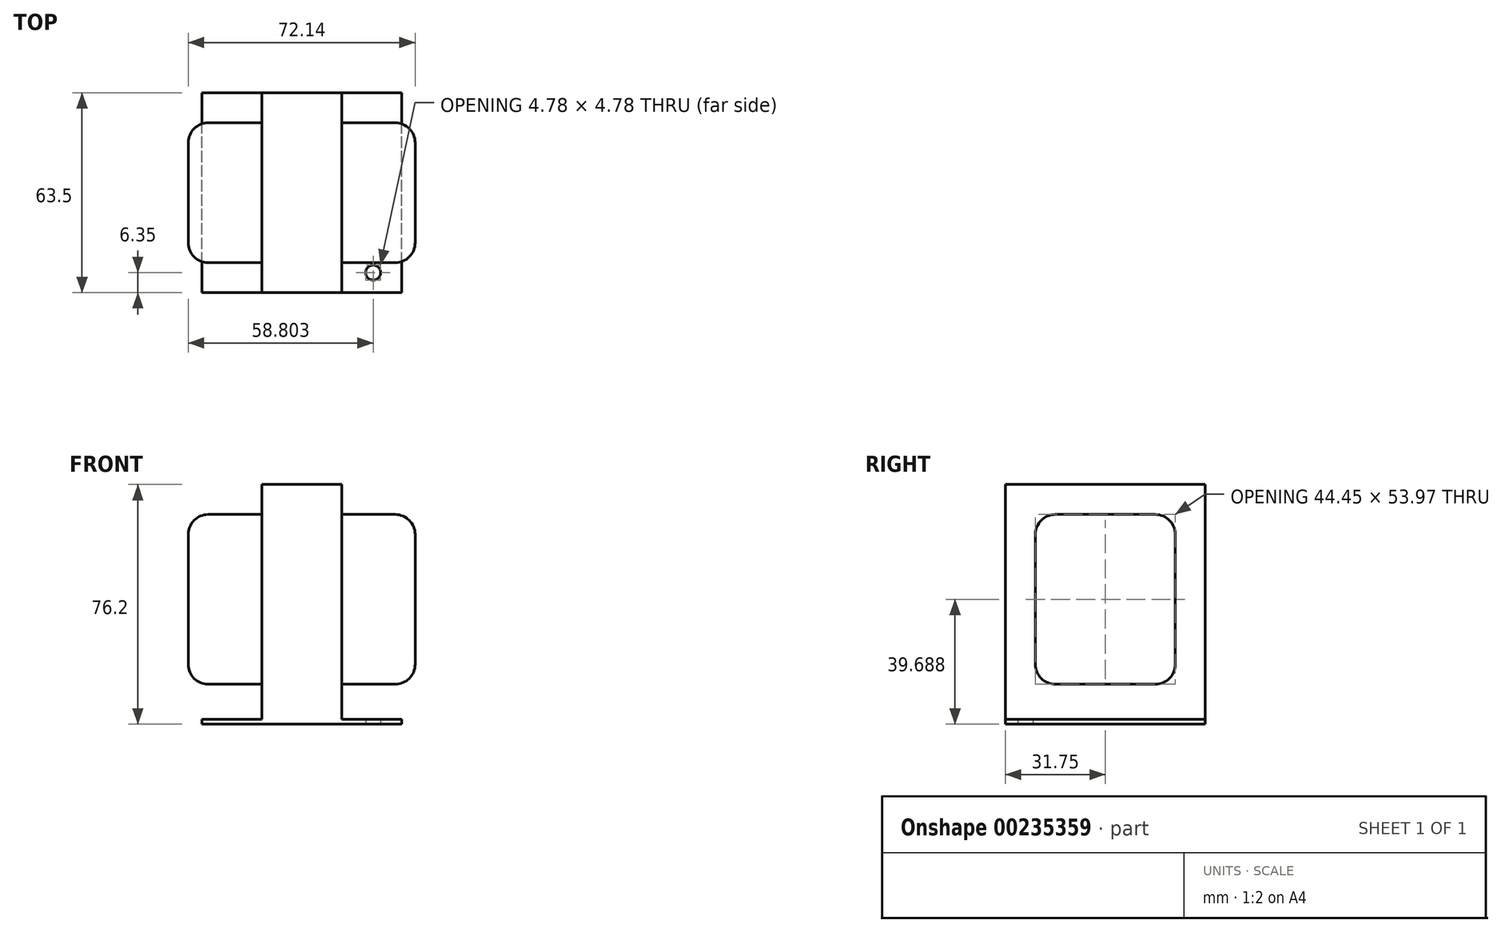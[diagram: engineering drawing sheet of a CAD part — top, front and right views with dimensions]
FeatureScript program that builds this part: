
annotation { "Feature Type Name" : "Feature", "Feature Type Description" : "" }
export const myFeature = defineFeature(function(context is Context, id is Id, definition is map)
    precondition{}
    {
        {
            var Q0;
            Q0=qCreatedBy(makeId("Front.planeOp"),FACE);
            var sketch = newSketch(context, id + "F0", { "sketchPlane" : qUnion([Q0])});
            skPoint(sketch, "E0.0", {"position": v(0, 0) * mm});
            skLineSegment(sketch, "E1.bottom", {"start": v(0, 0) * mm, "end": v(-31.75, 0) * mm});
            skLineSegment(sketch, "E1.top", {"start": v(0, 1.52) * mm, "end": v(-31.75, 1.52) * mm});
            skLineSegment(sketch, "E1.left", {"start": v(0, 0) * mm, "end": v(0, 1.52) * mm});
            skLineSegment(sketch, "E1.right", {"start": v(-31.75, 0) * mm, "end": v(-31.75, 1.52) * mm});
            skLineSegment(sketch, "E2.bottom", {"start": v(0, 0) * mm, "end": v(-12.7, 0) * mm});
            skLineSegment(sketch, "E2.top", {"start": v(0, 76.2) * mm, "end": v(-12.7, 76.2) * mm});
            skLineSegment(sketch, "E2.left", {"start": v(0, 0) * mm, "end": v(0, 76.2) * mm});
            skLineSegment(sketch, "E2.right", {"start": v(-12.7, 0) * mm, "end": v(-12.7, 76.2) * mm});
            skSolve(sketch);
        }
        {
            var Q0;
            {var subQ5=sQuery(id+"F0.wireOp",EDGE,"E2.top");Q0=makeQuery(id+"F0.imprint","IMPRINT",FACE,{"disambiguationData":[TD([[makeQuery(id+"F0.imprint","IMPRINT",EDGE,{"derivedFrom":subQ5}),1.0]])]});}
            var Q1;
            {var subQ0=sQuery(id+"F0.wireOp",EDGE,"E1.bottom");Q1=makeQuery(id+"F0.imprint","IMPRINT",FACE,{"disambiguationData":[TD([[makeQuery(id+"F0.imprint","IMPRINT",EDGE,{"derivedFrom":subQ0}),-1.0]])]});}
            var Q2;
            {var subQ5=sQuery(id+"F0.wireOp",EDGE,"E2.bottom");Q2=makeQuery(id+"F0.imprint","IMPRINT",FACE,{"disambiguationData":[TD([[makeQuery(id+"F0.imprint","IMPRINT",EDGE,{"derivedFrom":subQ5}),-1.0]])]});}
            extrude(context, id + "F1", {"entities" : qUnion([Q0, Q1, Q2]), "endBound" : BoundingType.SYMMETRIC, "depth" : 63.5 * mm});
        }
        {
            var Q0;
            Q0=makeQuery(id+"F1.opExtrude","SWEPT_BODY",BODY,{"disambiguationData":[OSD([sQuery(id+"F0.wireOp",EDGE,"E1.bottom"),sQuery(id+"F0.wireOp",EDGE,"E1.top"),sQuery(id+"F0.wireOp",EDGE,"E1.right"),sQuery(id+"F0.wireOp",EDGE,"E2.bottom"),sQuery(id+"F0.wireOp",EDGE,"E2.top"),sQuery(id+"F0.wireOp",EDGE,"E2.left"),sQuery(id+"F0.wireOp",EDGE,"E2.right")])]});
            var Q1;
            Q1=qCreatedBy(makeId("Right.planeOp"),FACE);
            mirror(context, id + "F2", {"operationType" : NewBodyOperationType.ADD, "entities" : qUnion([Q0]), "mirrorPlane" : qUnion([Q1])});
        }
        {
            var Q0;
            Q0=qCreatedBy(makeId("Right.planeOp"),FACE);
            var sketch = newSketch(context, id + "F3", { "sketchPlane" : qUnion([Q0])});
            skLineSegment(sketch, "E3.bottom", {"start": v(-22.23, 66.67) * mm, "end": v(22.23, 66.67) * mm});
            skLineSegment(sketch, "E3.top", {"start": v(-22.22, 12.7) * mm, "end": v(22.23, 12.7) * mm});
            skLineSegment(sketch, "E3.left", {"start": v(-22.23, 66.67) * mm, "end": v(-22.22, 12.7) * mm});
            skLineSegment(sketch, "E3.right", {"start": v(22.23, 66.67) * mm, "end": v(22.23, 12.7) * mm});
            skSolve(sketch);
        }
        {
            var Q0;
            Q0 = qSketchRegion(id + "F3", true);
            extrude(context, id + "F4", {"entities" : qUnion([Q0]), "operationType" : NewBodyOperationType.ADD, "endBound" : BoundingType.SYMMETRIC, "depth" : 72.14 * mm});
        }
        {
            var Q0;
            {var subQ0=makeQuery(id+"F1.opExtrude","SWEPT_FACE",FACE,{"disambiguationData":[OSD([sQuery(id+"F0.wireOp",EDGE,"E1.bottom"),sQuery(id+"F0.wireOp",EDGE,"E2.bottom")])]});Q0=makeQuery(id+"F2.boolean.opBoolean","MERGE",FACE,{"derivedFrom":[subQ0,makeQuery(id+"F2.opPattern","COPY",FACE,{"derivedFrom":subQ0,"instanceName":"1"})]});}
            var sketch = newSketch(context, id + "F5", { "sketchPlane" : qUnion([Q0])});
            skLineSegment(sketch, "E4.0.1", {"start": v(31.75, -31.75) * mm, "end": v(31.75, 31.75) * mm});
            skLineSegment(sketch, "E4.0.2", {"start": v(31.75, 31.75) * mm, "end": v(-31.75, 31.75) * mm});
            skLineSegment(sketch, "E5", {"start": v(-31.75, 0) * mm, "end": v(31.75, 0) * mm, "construction": true});
            skLineSegment(sketch, "E6.bottom", {"start": v(22.74, 23.01) * mm, "end": v(22.73, 23.01) * mm});
            skLineSegment(sketch, "E6.top", {"start": v(22.74, 27.79) * mm, "end": v(22.73, 27.79) * mm});
            skLineSegment(sketch, "E6.left", {"start": v(25.12, 25.4) * mm, "end": v(25.12, 25.4) * mm});
            skLineSegment(sketch, "E6.right", {"start": v(20.35, 25.4) * mm, "end": v(20.35, 25.4) * mm});
            skPoint(sketch, "E6.middle", {"position": v(22.73, 25.4) * mm});
            skPoint(sketch, "E7.visualSharp", {"position": v(20.35, 23.01) * mm});
            skArc(sketch, "E7.filletArc", {"start": v(20.35, 25.4) * mm, "mid": v(21.04, 23.7) * mm, "end": v(22.73, 23.01) * mm});
            skPoint(sketch, "E8.visualSharp", {"position": v(20.35, 27.79) * mm});
            skArc(sketch, "E8.filletArc", {"start": v(22.73, 27.79) * mm, "mid": v(21.04, 27.1) * mm, "end": v(20.35, 25.4) * mm});
            skPoint(sketch, "E9.visualSharp", {"position": v(25.12, 27.79) * mm});
            skArc(sketch, "E9.filletArc", {"start": v(25.12, 25.4) * mm, "mid": v(24.42, 27.1) * mm, "end": v(22.74, 27.79) * mm});
            skPoint(sketch, "E10.visualSharp", {"position": v(25.12, 23.01) * mm});
            skArc(sketch, "E10.filletArc", {"start": v(22.74, 23.01) * mm, "mid": v(24.42, 23.7) * mm, "end": v(25.12, 25.4) * mm});
            skSolve(sketch);
        }
        {
            var Q0;
            Q0=makeQuery(id+"F5.imprint","IMPRINT",FACE,{"disambiguationData":[TD([[makeQuery(id+"F5.imprint","IMPRINT",EDGE,{"derivedFrom":sQuery(id+"F5.wireOp",EDGE,"E6.bottom")}),-1.0]])]});
            extrude(context, id + "F6", {"entities" : qUnion([Q0]), "operationType" : NewBodyOperationType.REMOVE, "endBound" : BoundingType.UP_TO_NEXT, "oppositeDirection" : true, "depth" : 25.4 * mm});
        }
        {
            var Q0;
            {var subQ0=sQuery(id+"F3.wireOp",EDGE,"E3.left");var subQ1=sQuery(id+"F3.wireOp",EDGE,"E3.bottom");Q0=makeQuery(id+"F4.boolean.opBoolean","SPLIT",EDGE,{"disambiguationData":[TD([makeQuery(id+"F2.opPattern","COPY",FACE,{"derivedFrom":makeQuery(id+"F1.opExtrude","SWEPT_FACE",FACE,{"disambiguationData":[OSD([sQuery(id+"F0.wireOp",EDGE,"E2.right")])]}),"instanceName":"1"})])],"derivedFrom":makeQuery(id+"F4.opExtrude","SWEPT_EDGE",EDGE,{"disambiguationData":[OSD([subQ1,subQ0])]})});}
            var Q1;
            {var subQ0=sQuery(id+"F3.wireOp",EDGE,"E3.right");var subQ1=sQuery(id+"F3.wireOp",EDGE,"E3.bottom");Q1=makeQuery(id+"F4.boolean.opBoolean","SPLIT",EDGE,{"disambiguationData":[TD([makeQuery(id+"F2.opPattern","COPY",FACE,{"derivedFrom":makeQuery(id+"F1.opExtrude","SWEPT_FACE",FACE,{"disambiguationData":[OSD([sQuery(id+"F0.wireOp",EDGE,"E2.right")])]}),"instanceName":"1"})])],"derivedFrom":makeQuery(id+"F4.opExtrude","SWEPT_EDGE",EDGE,{"disambiguationData":[OSD([subQ1,subQ0])]})});}
            var Q2;
            {var subQ0=sQuery(id+"F3.wireOp",EDGE,"E3.right");var subQ1=sQuery(id+"F3.wireOp",EDGE,"E3.top");Q2=makeQuery(id+"F4.boolean.opBoolean","SPLIT",EDGE,{"disambiguationData":[TD([makeQuery(id+"F2.opPattern","COPY",FACE,{"derivedFrom":makeQuery(id+"F1.opExtrude","SWEPT_FACE",FACE,{"disambiguationData":[OSD([sQuery(id+"F0.wireOp",EDGE,"E2.right")])]}),"instanceName":"1"})])],"derivedFrom":makeQuery(id+"F4.opExtrude","SWEPT_EDGE",EDGE,{"disambiguationData":[OSD([subQ1,subQ0])]})});}
            var Q3;
            {var subQ0=sQuery(id+"F3.wireOp",EDGE,"E3.left");var subQ1=sQuery(id+"F3.wireOp",EDGE,"E3.top");Q3=makeQuery(id+"F4.boolean.opBoolean","SPLIT",EDGE,{"disambiguationData":[TD([makeQuery(id+"F2.opPattern","COPY",FACE,{"derivedFrom":makeQuery(id+"F1.opExtrude","SWEPT_FACE",FACE,{"disambiguationData":[OSD([sQuery(id+"F0.wireOp",EDGE,"E2.right")])]}),"instanceName":"1"})])],"derivedFrom":makeQuery(id+"F4.opExtrude","SWEPT_EDGE",EDGE,{"disambiguationData":[OSD([subQ1,subQ0])]})});}
            var Q4;
            {var subQ0=sQuery(id+"F3.wireOp",EDGE,"E3.left");var subQ1=sQuery(id+"F3.wireOp",EDGE,"E3.top");Q4=makeQuery(id+"F4.boolean.opBoolean","SPLIT",EDGE,{"disambiguationData":[TD([makeQuery(id+"F1.opExtrude","SWEPT_FACE",FACE,{"disambiguationData":[OSD([sQuery(id+"F0.wireOp",EDGE,"E2.right")])]})])],"derivedFrom":makeQuery(id+"F4.opExtrude","SWEPT_EDGE",EDGE,{"disambiguationData":[OSD([subQ1,subQ0])]})});}
            var Q5;
            {var subQ0=sQuery(id+"F3.wireOp",EDGE,"E3.bottom");var subQ1=sQuery(id+"F3.wireOp",EDGE,"E3.left");Q5=makeQuery(id+"F4.boolean.opBoolean","SPLIT",EDGE,{"disambiguationData":[TD([makeQuery(id+"F1.opExtrude","SWEPT_FACE",FACE,{"disambiguationData":[OSD([sQuery(id+"F0.wireOp",EDGE,"E2.right")])]})])],"derivedFrom":makeQuery(id+"F4.opExtrude","SWEPT_EDGE",EDGE,{"disambiguationData":[OSD([subQ0,subQ1])]})});}
            var Q6;
            {var subQ0=sQuery(id+"F3.wireOp",EDGE,"E3.bottom");var subQ1=sQuery(id+"F3.wireOp",EDGE,"E3.right");Q6=makeQuery(id+"F4.boolean.opBoolean","SPLIT",EDGE,{"disambiguationData":[TD([makeQuery(id+"F1.opExtrude","SWEPT_FACE",FACE,{"disambiguationData":[OSD([sQuery(id+"F0.wireOp",EDGE,"E2.right")])]})])],"derivedFrom":makeQuery(id+"F4.opExtrude","SWEPT_EDGE",EDGE,{"disambiguationData":[OSD([subQ0,subQ1])]})});}
            var Q7;
            {var subQ0=sQuery(id+"F3.wireOp",EDGE,"E3.right");var subQ1=sQuery(id+"F3.wireOp",EDGE,"E3.top");Q7=makeQuery(id+"F4.boolean.opBoolean","SPLIT",EDGE,{"disambiguationData":[TD([makeQuery(id+"F1.opExtrude","SWEPT_FACE",FACE,{"disambiguationData":[OSD([sQuery(id+"F0.wireOp",EDGE,"E2.right")])]})])],"derivedFrom":makeQuery(id+"F4.opExtrude","SWEPT_EDGE",EDGE,{"disambiguationData":[OSD([subQ1,subQ0])]})});}
            fillet(context, id + "F7", {"entities" : qUnion([Q0, Q1, Q2, Q3, Q4, Q5, Q6, Q7]), "radius" : 6.35 * mm, "tangentPropagation" : true, "allowEdgeOverflow" : false});
        }
        {
            var Q0;
            Q0=makeQuery(id+"F4.opExtrude","CAP_FACE",FACE,{"disambiguationData":[OSD([sQuery(id+"F3.wireOp",EDGE,"E3.bottom"),sQuery(id+"F3.wireOp",EDGE,"E3.top"),sQuery(id+"F3.wireOp",EDGE,"E3.left"),sQuery(id+"F3.wireOp",EDGE,"E3.right")])],"isStart":true});
            var Q1;
            Q1=makeQuery(id+"F4.opExtrude","CAP_FACE",FACE,{"disambiguationData":[OSD([sQuery(id+"F3.wireOp",EDGE,"E3.bottom"),sQuery(id+"F3.wireOp",EDGE,"E3.top"),sQuery(id+"F3.wireOp",EDGE,"E3.left"),sQuery(id+"F3.wireOp",EDGE,"E3.right")])],"isStart":false});
            fillet(context, id + "F8", {"entities" : qUnion([Q0, Q1]), "radius" : 6.35 * mm, "tangentPropagation" : true, "allowEdgeOverflow" : false});
        }
    });
